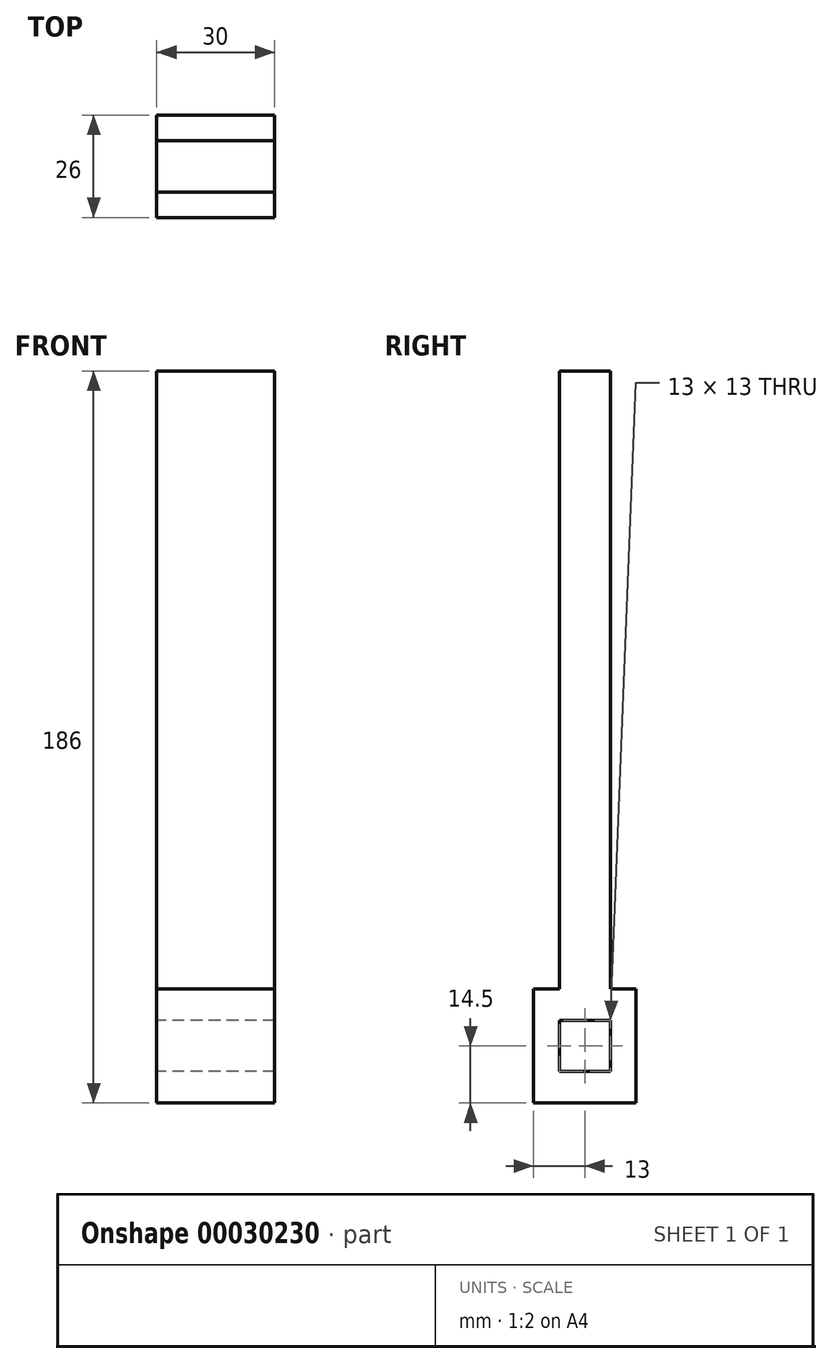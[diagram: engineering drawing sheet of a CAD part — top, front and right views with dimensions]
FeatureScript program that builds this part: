
annotation { "Feature Type Name" : "Feature", "Feature Type Description" : "" }
export const myFeature = defineFeature(function(context is Context, id is Id, definition is map)
    precondition{}
    {
        {
            var Q0;
            Q0=qCreatedBy(makeId("Top.planeOp"),FACE);
            var sketch = newSketch(context, id + "F0", { "sketchPlane" : qUnion([Q0])});
            skLineSegment(sketch, "E0.rect.bottom", {"start": v(15, -6.5) * mm, "end": v(-15, -6.5) * mm});
            skLineSegment(sketch, "E0.rect.top", {"start": v(15, 6.5) * mm, "end": v(-15, 6.5) * mm});
            skLineSegment(sketch, "E0.rect.left", {"start": v(15, -6.5) * mm, "end": v(15, 6.5) * mm});
            skLineSegment(sketch, "E0.rect.right", {"start": v(-15, -6.5) * mm, "end": v(-15, 6.5) * mm});
            skPoint(sketch, "E0.rect.middle", {"position": v(0, 0) * mm});
            skSolve(sketch);
        }
        {
            var Q0;
            Q0 = qSketchRegion(id + "F0", true);
            extrude(context, id + "F1", {"entities" : qUnion([Q0]), "depth" : 157 * mm});
        }
        {
            var Q0;
            Q0=makeQuery(id+"F1.opExtrude","CAP_FACE",FACE,{"disambiguationData":[OSD([sQuery(id+"F0.wireOp",EDGE,"E0.rect.bottom"),sQuery(id+"F0.wireOp",EDGE,"E0.rect.top"),sQuery(id+"F0.wireOp",EDGE,"E0.rect.left"),sQuery(id+"F0.wireOp",EDGE,"E0.rect.right")])],"isStart":true});
            var sketch = newSketch(context, id + "F2", { "sketchPlane" : qUnion([Q0])});
            skLineSegment(sketch, "E1.rect.bottom", {"start": v(15, -13) * mm, "end": v(-15, -13) * mm});
            skLineSegment(sketch, "E1.rect.top", {"start": v(15, 13) * mm, "end": v(-15, 13) * mm});
            skLineSegment(sketch, "E1.rect.left", {"start": v(15, -13) * mm, "end": v(15, 13) * mm});
            skLineSegment(sketch, "E1.rect.right", {"start": v(-15, -13) * mm, "end": v(-15, 13) * mm});
            skPoint(sketch, "E1.rect.middle", {"position": v(0, 0) * mm});
            skSolve(sketch);
        }
        {
            var Q0;
            Q0 = qSketchRegion(id + "F2", true);
            extrude(context, id + "F3", {"entities" : qUnion([Q0]), "operationType" : NewBodyOperationType.ADD, "depth" : 8 * mm});
        }
        {
            var Q0;
            Q0=makeQuery(id+"F3.opExtrude","CAP_FACE",FACE,{"disambiguationData":[OSD([sQuery(id+"F2.wireOp",EDGE,"E1.rect.bottom"),sQuery(id+"F2.wireOp",EDGE,"E1.rect.top"),sQuery(id+"F2.wireOp",EDGE,"E1.rect.left"),sQuery(id+"F2.wireOp",EDGE,"E1.rect.right")])],"isStart":false});
            var sketch = newSketch(context, id + "F4", { "sketchPlane" : qUnion([Q0])});
            skLineSegment(sketch, "E2.rect.bottom", {"start": v(15, -13) * mm, "end": v(-15, -13) * mm});
            skLineSegment(sketch, "E2.rect.top", {"start": v(15, -6.5) * mm, "end": v(-15, -6.5) * mm});
            skLineSegment(sketch, "E2.rect.left", {"start": v(15, -13) * mm, "end": v(15, -6.5) * mm});
            skLineSegment(sketch, "E2.rect.right", {"start": v(-15, -13) * mm, "end": v(-15, -6.5) * mm});
            skPoint(sketch, "E2.rect.middle", {"position": v(0, -9.75) * mm});
            skLineSegment(sketch, "E3.rect.bottom", {"start": v(15, 13) * mm, "end": v(-15, 13) * mm});
            skLineSegment(sketch, "E3.rect.top", {"start": v(15, 6.5) * mm, "end": v(-15, 6.5) * mm});
            skLineSegment(sketch, "E3.rect.left", {"start": v(15, 13) * mm, "end": v(15, 6.5) * mm});
            skLineSegment(sketch, "E3.rect.right", {"start": v(-15, 13) * mm, "end": v(-15, 6.5) * mm});
            skPoint(sketch, "E3.rect.middle", {"position": v(0, 9.75) * mm});
            skSolve(sketch);
        }
        {
            var Q0;
            Q0 = qSketchRegion(id + "F4", true);
            extrude(context, id + "F5", {"entities" : qUnion([Q0]), "operationType" : NewBodyOperationType.ADD, "depth" : 13 * mm});
        }
        {
            var Q0;
            Q0=makeQuery(id+"F5.opExtrude","CAP_FACE",FACE,{"disambiguationData":[OSD([sQuery(id+"F4.wireOp",EDGE,"E3.rect.bottom"),sQuery(id+"F4.wireOp",EDGE,"E3.rect.top"),sQuery(id+"F4.wireOp",EDGE,"E3.rect.left"),sQuery(id+"F4.wireOp",EDGE,"E3.rect.right")])],"isStart":false});
            var sketch = newSketch(context, id + "F6", { "sketchPlane" : qUnion([Q0])});
            skLineSegment(sketch, "E4.bottom", {"start": v(-15, 13) * mm, "end": v(15, 13) * mm});
            skLineSegment(sketch, "E4.top", {"start": v(-15, -13) * mm, "end": v(15, -13) * mm});
            skLineSegment(sketch, "E4.left", {"start": v(-15, 13) * mm, "end": v(-15, -13) * mm});
            skLineSegment(sketch, "E4.right", {"start": v(15, 13) * mm, "end": v(15, -13) * mm});
            skSolve(sketch);
        }
        {
            var Q0;
            Q0 = qSketchRegion(id + "F6", true);
            extrude(context, id + "F7", {"entities" : qUnion([Q0]), "operationType" : NewBodyOperationType.ADD, "depth" : 8 * mm});
        }
    });
